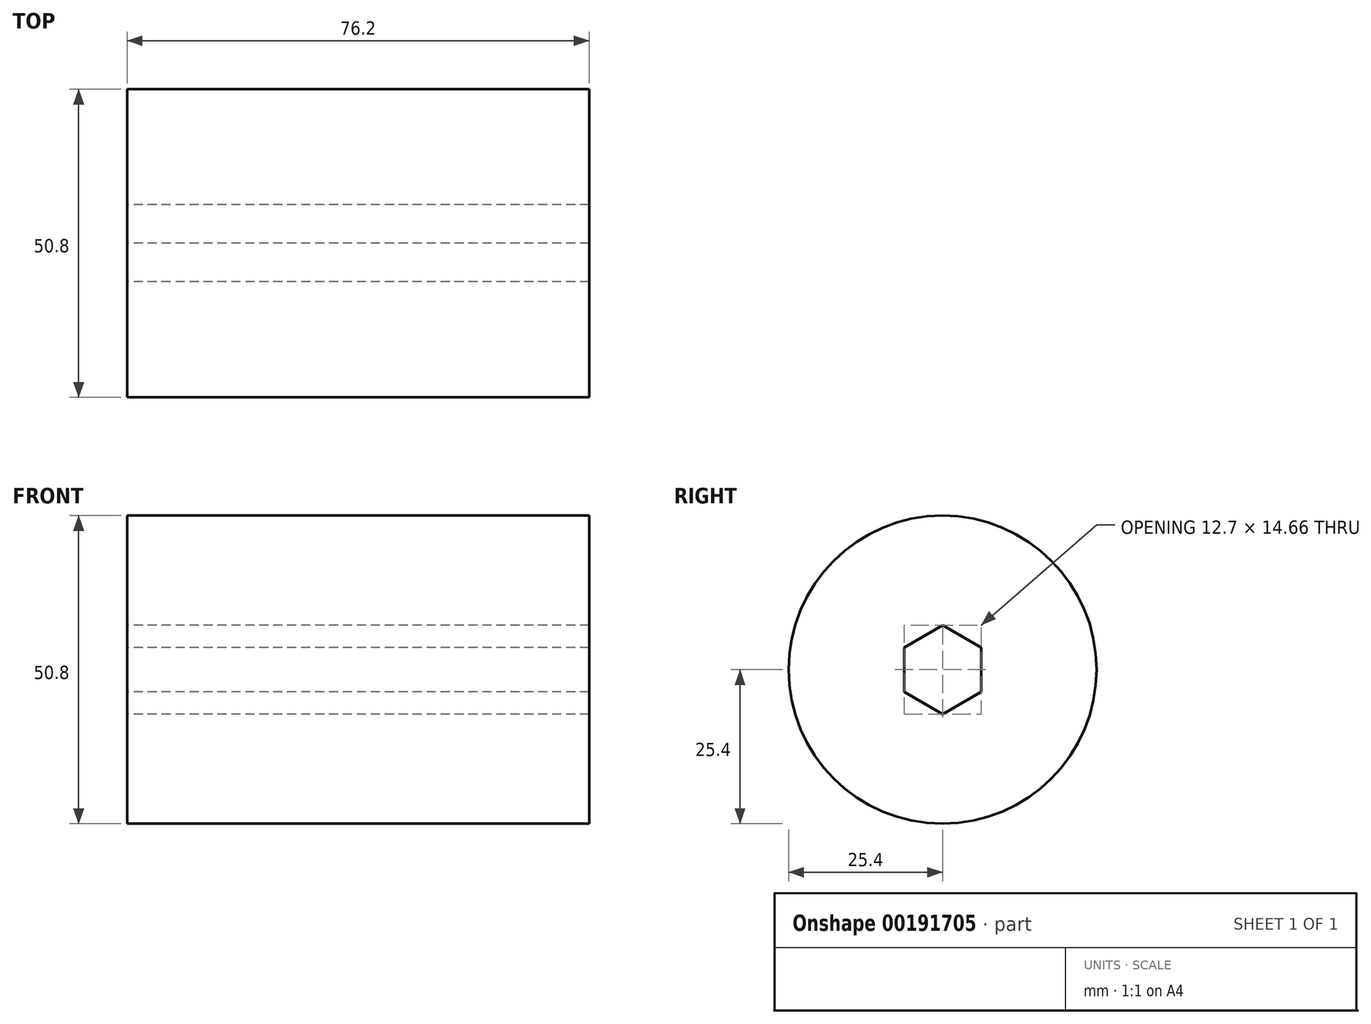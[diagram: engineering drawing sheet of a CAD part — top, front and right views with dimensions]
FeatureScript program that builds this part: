
annotation { "Feature Type Name" : "Feature", "Feature Type Description" : "" }
export const myFeature = defineFeature(function(context is Context, id is Id, definition is map)
    precondition{}
    {
        {
            var Q0;
            Q0=qCreatedBy(makeId("Right.planeOp"),FACE);
            var sketch = newSketch(context, id + "F0", { "sketchPlane" : qUnion([Q0])});
            skCircle(sketch, "E0", {"center": v(0, 0) * mm, "radius": 25.4 * mm});
            skCircle(sketch, "E1.cCircle", {"center": v(0, 0) * mm, "radius": 6.35 * mm, "construction": true});
            skLineSegment(sketch, "E1.0", {"start": v(6.35, 3.67) * mm, "end": v(6.35, -3.67) * mm});
            skLineSegment(sketch, "E1.1", {"start": v(6.35, -3.67) * mm, "end": v(0, -7.33) * mm});
            skLineSegment(sketch, "E1.2", {"start": v(0, -7.33) * mm, "end": v(-6.35, -3.67) * mm});
            skLineSegment(sketch, "E1.3", {"start": v(-6.35, -3.67) * mm, "end": v(-6.35, 3.67) * mm});
            skLineSegment(sketch, "E1.4", {"start": v(-6.35, 3.67) * mm, "end": v(0, 7.33) * mm});
            skLineSegment(sketch, "E1.5", {"start": v(0, 7.33) * mm, "end": v(6.35, 3.67) * mm});
            skPoint(sketch, "E1.0.midPoint", {"position": v(6.35, 0) * mm});
            skSolve(sketch);
        }
        {
            var Q0;
            Q0=makeQuery(id+"F0.imprint","IMPRINT",FACE,{"disambiguationData":[TD([[makeQuery(id+"F0.imprint","IMPRINT",EDGE,{"derivedFrom":sQuery(id+"F0.wireOp",EDGE,"E0")}),1.0]])]});
            extrude(context, id + "F1", {"entities" : qUnion([Q0]), "depth" : 76.2 * mm});
        }
    });
